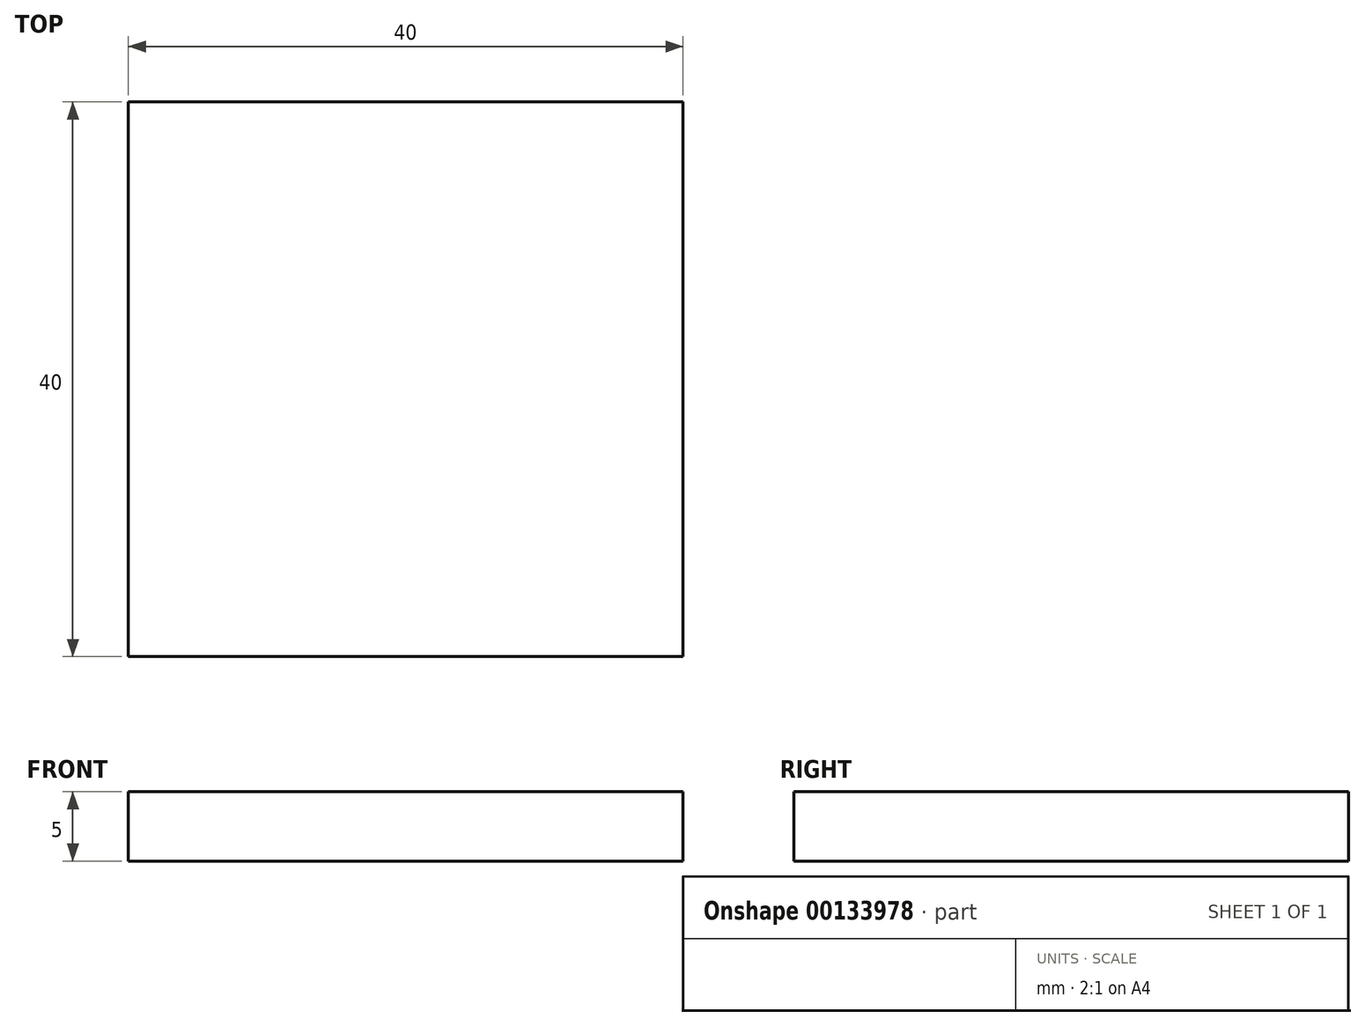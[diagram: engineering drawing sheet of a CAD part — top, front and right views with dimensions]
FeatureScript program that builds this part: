
annotation { "Feature Type Name" : "Feature", "Feature Type Description" : "" }
export const myFeature = defineFeature(function(context is Context, id is Id, definition is map)
    precondition{}
    {
        {
            var Q0;
            Q0=qCreatedBy(makeId("Top.planeOp"),FACE);
            var sketch = newSketch(context, id + "F0", { "sketchPlane" : qUnion([Q0])});
            skLineSegment(sketch, "E0.bottom", {"start": v(20, -20) * mm, "end": v(-20, -20) * mm});
            skLineSegment(sketch, "E0.top", {"start": v(20, 20) * mm, "end": v(-20, 20) * mm});
            skLineSegment(sketch, "E0.left", {"start": v(20, -20) * mm, "end": v(20, 20) * mm});
            skLineSegment(sketch, "E0.right", {"start": v(-20, -20) * mm, "end": v(-20, 20) * mm});
            skPoint(sketch, "E0.middle", {"position": v(0, 0) * mm});
            skSolve(sketch);
        }
        {
            var Q0;
            Q0=makeQuery(id+"F0.imprint","IMPRINT",FACE,{"disambiguationData":[TD([[makeQuery(id+"F0.imprint","IMPRINT",EDGE,{"derivedFrom":sQuery(id+"F0.wireOp",EDGE,"E0.bottom")}),-1.0]])]});
            extrude(context, id + "F1", {"entities" : qUnion([Q0]), "depth" : 5 * mm, "offsetDistance" : 25 * mm});
        }
    });
